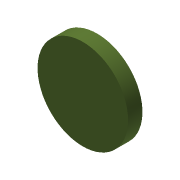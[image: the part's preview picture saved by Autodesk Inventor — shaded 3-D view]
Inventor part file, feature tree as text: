
AUTODESK INVENTOR PART (.ipt)
format: ipt  version: 2014 (Build 180170000, 170)  size: 82,432 bytes
history: native  units: mm
features: extrude x2, sketch x2
ambient origin geometry x8: Origin, YZ Plane, XZ Plane, XY Plane, X Axis, Y Axis, Z Axis, Center Point
bodies: Solid1 (feature_tree)
feature tree (4):
  extrude  "Extrusion1"  Depth=4.0mm
  extrude  "Extrusion2"  Depth=4.0mm TaperAngle=0.0deg
  sketch  "Sketch1"  dims[d0=120.0mm d1=4.0mm]
  sketch  "Sketch2"  dims[d2=15.0mm d3=0.0mm d4=4.0mm d5=0.0mm]
